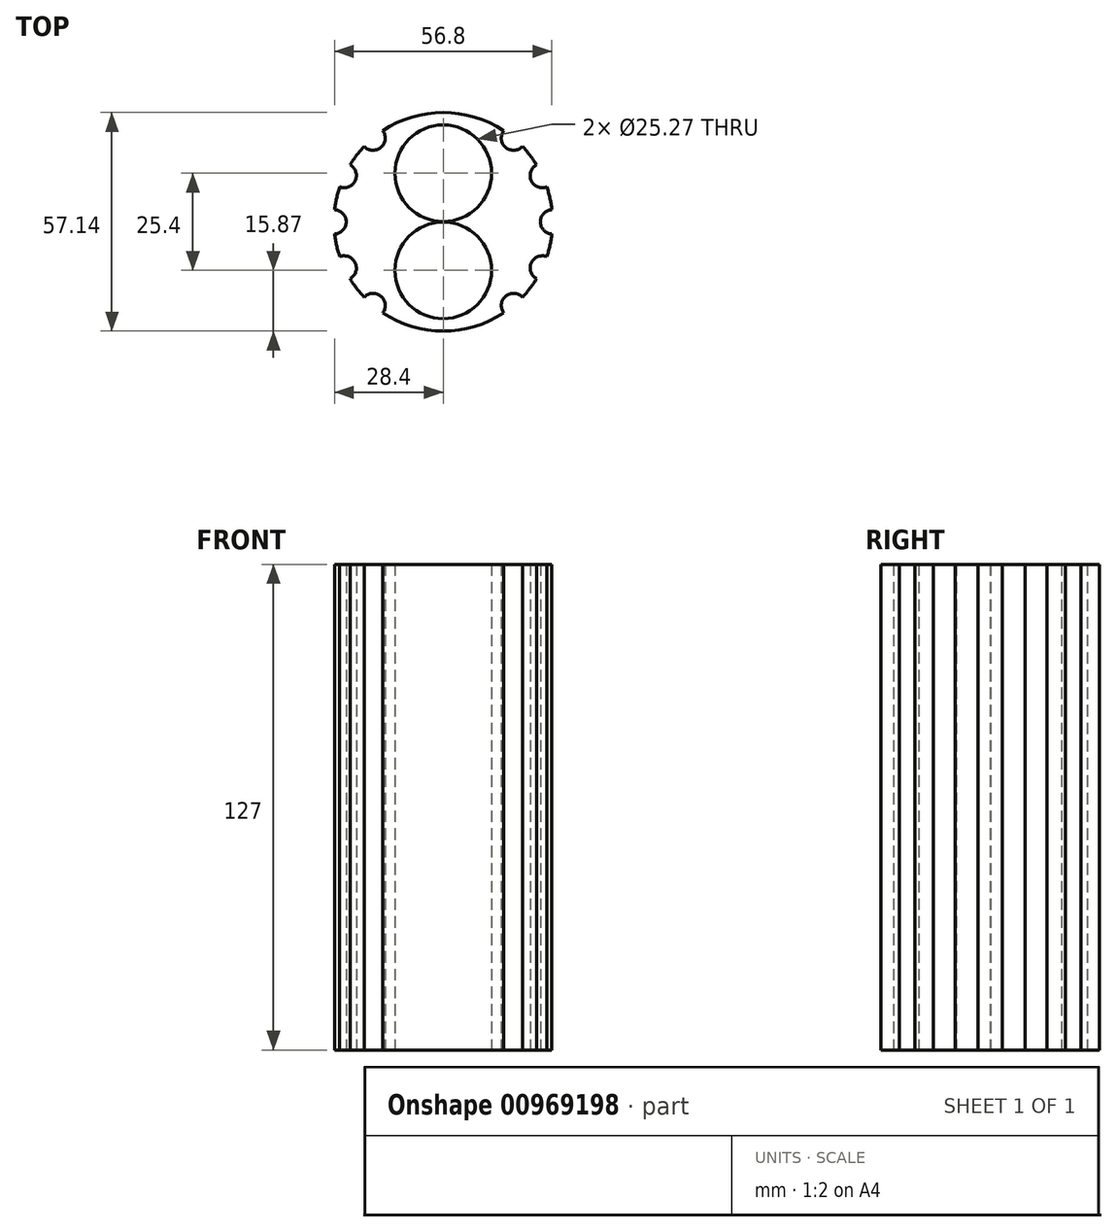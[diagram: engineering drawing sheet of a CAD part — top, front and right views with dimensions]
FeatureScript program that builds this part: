
annotation { "Feature Type Name" : "Feature", "Feature Type Description" : "" }
export const myFeature = defineFeature(function(context is Context, id is Id, definition is map)
    precondition{}
    {
        {
            var Q0;
            Q0=qCreatedBy(makeId("Top.planeOp"),FACE);
            var sketch = newSketch(context, id + "F0", { "sketchPlane" : qUnion([Q0])});
            skCircle(sketch, "E0", {"center": v(0, 0) * mm, "radius": 28.58 * mm});
            skPoint(sketch, "E1", {"position": v(0, -12.7) * mm});
            skPoint(sketch, "E2", {"position": v(0, 12.7) * mm});
            skCircle(sketch, "E3", {"center": v(0, -12.7) * mm, "radius": 12.64 * mm});
            skCircle(sketch, "E4", {"center": v(0, 12.7) * mm, "radius": 12.64 * mm});
            skSolve(sketch);
        }
        {
            var Q0;
            Q0 = qSketchRegion(id + "F0", true);
            extrude(context, id + "F1", {"entities" : qUnion([Q0]), "endBound" : BoundingType.SYMMETRIC, "depth" : 127 * mm, "offsetDistance" : 25.4 * mm});
        }
        {
            var Q0;
            Q0=qCreatedBy(makeId("Top.planeOp"),FACE);
            cPlane(context, id + "F2", {"entities" : qUnion([Q0]), "cplaneType" : CPlaneType.OFFSET, "offset" : 63.5 * mm, "oppositeDirection" : true, "width" : 152.4 * mm, "height" : 152.4 * mm});
        }
        {
            var Q0;
            Q0=qCreatedBy(id+"F2.planeOp",FACE);
            var sketch = newSketch(context, id + "F3", { "sketchPlane" : qUnion([Q0])});
            skPoint(sketch, "E5", {"position": v(28.58, 0) * mm});
            skPoint(sketch, "E6", {"position": v(25.9, -12.08) * mm});
            skPoint(sketch, "E7", {"position": v(25.9, 12.08) * mm});
            skLineSegment(sketch, "E8", {"start": v(0, 0) * mm, "end": v(28.58, 0) * mm, "construction": true});
            skLineSegment(sketch, "E9", {"start": v(0, 0) * mm, "end": v(25.9, -12.08) * mm, "construction": true});
            skLineSegment(sketch, "E10", {"start": v(0, 0) * mm, "end": v(25.9, 12.08) * mm, "construction": true});
            skPoint(sketch, "E11", {"position": v(18.37, -21.89) * mm});
            skPoint(sketch, "E12", {"position": v(18.37, 21.89) * mm});
            skLineSegment(sketch, "E13", {"start": v(0, 0) * mm, "end": v(18.37, -21.89) * mm, "construction": true});
            skLineSegment(sketch, "E14", {"start": v(0, 0) * mm, "end": v(18.37, 21.89) * mm, "construction": true});
            skArc(sketch, "E15", {"start": v(20.68, -19.72) * mm, "mid": v(16.33, -19.46) * mm, "end": v(15.83, -23.8) * mm});
            skArc(sketch, "E16", {"start": v(27.08, -9.13) * mm, "mid": v(23.02, -10.73) * mm, "end": v(24.4, -14.87) * mm});
            skArc(sketch, "E17", {"start": v(28.4, 3.17) * mm, "mid": v(25.4, 0) * mm, "end": v(28.4, -3.17) * mm});
            skArc(sketch, "E18", {"start": v(24.4, 14.87) * mm, "mid": v(23.02, 10.73) * mm, "end": v(27.08, 9.13) * mm});
            skArc(sketch, "E19", {"start": v(15.83, 23.8) * mm, "mid": v(16.33, 19.46) * mm, "end": v(20.68, 19.72) * mm});
            skArc(sketch, "E20", {"start": v(28.4, -3.17) * mm, "mid": v(28.58, 0) * mm, "end": v(28.4, 3.17) * mm});
            skArc(sketch, "E21.trimOffspring", {"start": v(27.08, 9.13) * mm, "mid": v(25.9, 12.08) * mm, "end": v(24.4, 14.87) * mm});
            skArc(sketch, "E22.trimOffspring", {"start": v(20.68, 19.72) * mm, "mid": v(18.37, 21.89) * mm, "end": v(15.83, 23.8) * mm});
            skArc(sketch, "E23.trimOffspring", {"start": v(15.83, -23.8) * mm, "mid": v(18.37, -21.89) * mm, "end": v(20.68, -19.72) * mm});
            skArc(sketch, "E24.trimOffspring", {"start": v(24.4, -14.87) * mm, "mid": v(25.9, -12.08) * mm, "end": v(27.08, -9.13) * mm});
            skArc(sketch, "E25.MirrorCS", {"start": v(-15.83, 23.8) * mm, "mid": v(-16.33, 19.46) * mm, "end": v(-20.68, 19.72) * mm});
            skArc(sketch, "E26.MirrorCS", {"start": v(-24.4, 14.87) * mm, "mid": v(-23.02, 10.73) * mm, "end": v(-27.08, 9.13) * mm});
            skArc(sketch, "E27.MirrorCS", {"start": v(-28.4, 3.17) * mm, "mid": v(-25.4, 0) * mm, "end": v(-28.4, -3.17) * mm});
            skArc(sketch, "E28.MirrorCS", {"start": v(-27.08, -9.13) * mm, "mid": v(-23.02, -10.73) * mm, "end": v(-24.4, -14.87) * mm});
            skArc(sketch, "E29.MirrorCS", {"start": v(-20.68, -19.72) * mm, "mid": v(-16.33, -19.46) * mm, "end": v(-15.83, -23.8) * mm});
            skArc(sketch, "E30.MirrorCS", {"start": v(-15.83, -23.8) * mm, "mid": v(-18.37, -21.89) * mm, "end": v(-20.68, -19.72) * mm});
            skArc(sketch, "E31", {"start": v(-15.83, 23.8) * mm, "mid": v(-18.37, 21.89) * mm, "end": v(-20.68, 19.72) * mm});
            skArc(sketch, "E32.trimOffspring", {"start": v(-20.68, -19.72) * mm, "mid": v(-18.37, -21.89) * mm, "end": v(-15.83, -23.8) * mm});
            skArc(sketch, "E33.trimOffspring", {"start": v(-27.08, -9.13) * mm, "mid": v(-25.9, -12.08) * mm, "end": v(-24.4, -14.87) * mm});
            skArc(sketch, "E34.trimOffspring", {"start": v(-28.4, 3.17) * mm, "mid": v(-28.58, 0) * mm, "end": v(-28.4, -3.17) * mm});
            skArc(sketch, "E35.trimOffspring", {"start": v(-24.4, 14.87) * mm, "mid": v(-25.9, 12.08) * mm, "end": v(-27.08, 9.13) * mm});
            skSolve(sketch);
        }
        {
            var Q0;
            Q0 = qSketchRegion(id + "F3", true);
            extrude(context, id + "F4", {"entities" : qUnion([Q0]), "operationType" : NewBodyOperationType.REMOVE, "depth" : 127 * mm, "offsetDistance" : 25.4 * mm});
        }
    });
